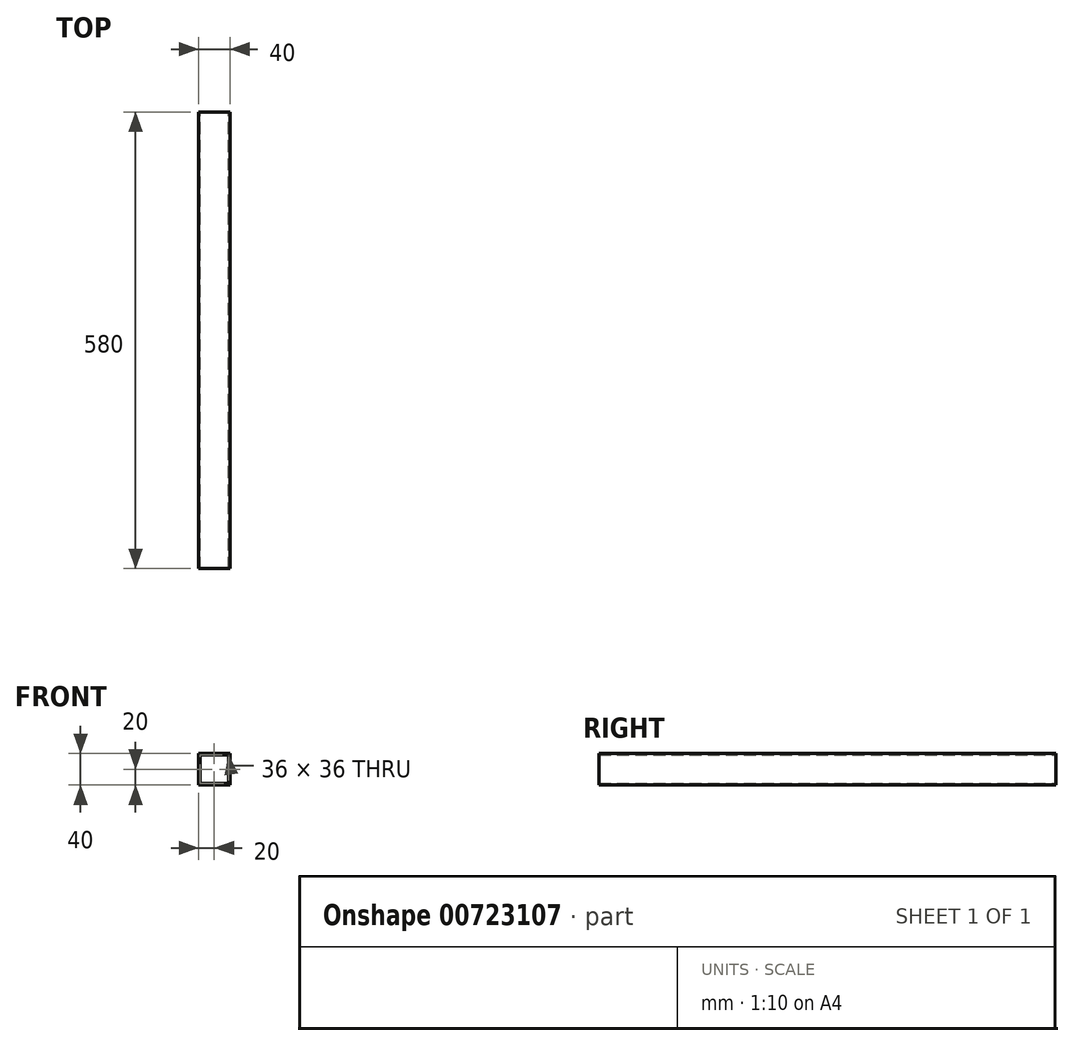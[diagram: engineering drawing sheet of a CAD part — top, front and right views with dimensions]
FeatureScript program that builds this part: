
annotation { "Feature Type Name" : "Feature", "Feature Type Description" : "" }
export const myFeature = defineFeature(function(context is Context, id is Id, definition is map)
    precondition{}
    {
        {
            var Q0;
            Q0=qCreatedBy(makeId("Front.planeOp"),FACE);
            var sketch = newSketch(context, id + "F0", { "sketchPlane" : qUnion([Q0])});
            skLineSegment(sketch, "E0.bottom", {"start": v(0, 0) * mm, "end": v(40, 0) * mm});
            skLineSegment(sketch, "E0.top", {"start": v(0, 40) * mm, "end": v(40, 40) * mm});
            skLineSegment(sketch, "E0.left", {"start": v(0, 0) * mm, "end": v(0, 40) * mm});
            skLineSegment(sketch, "E0.right", {"start": v(40, 0) * mm, "end": v(40, 40) * mm});
            skLineSegment(sketch, "E1.bottom", {"start": v(2, 2) * mm, "end": v(38, 2) * mm});
            skLineSegment(sketch, "E1.top", {"start": v(2, 38) * mm, "end": v(38, 38) * mm});
            skLineSegment(sketch, "E1.left", {"start": v(2, 2) * mm, "end": v(2, 38) * mm});
            skLineSegment(sketch, "E1.right", {"start": v(38, 2) * mm, "end": v(38, 38) * mm});
            skSolve(sketch);
        }
        {
            var Q0;
            Q0=qSketchRegion(id+"F0",true);
            extrude(context, id + "F1", {"entities" : qUnion([Q0]), "depth" : 580 * mm, "offsetDistance" : 25 * mm});
        }
    });
